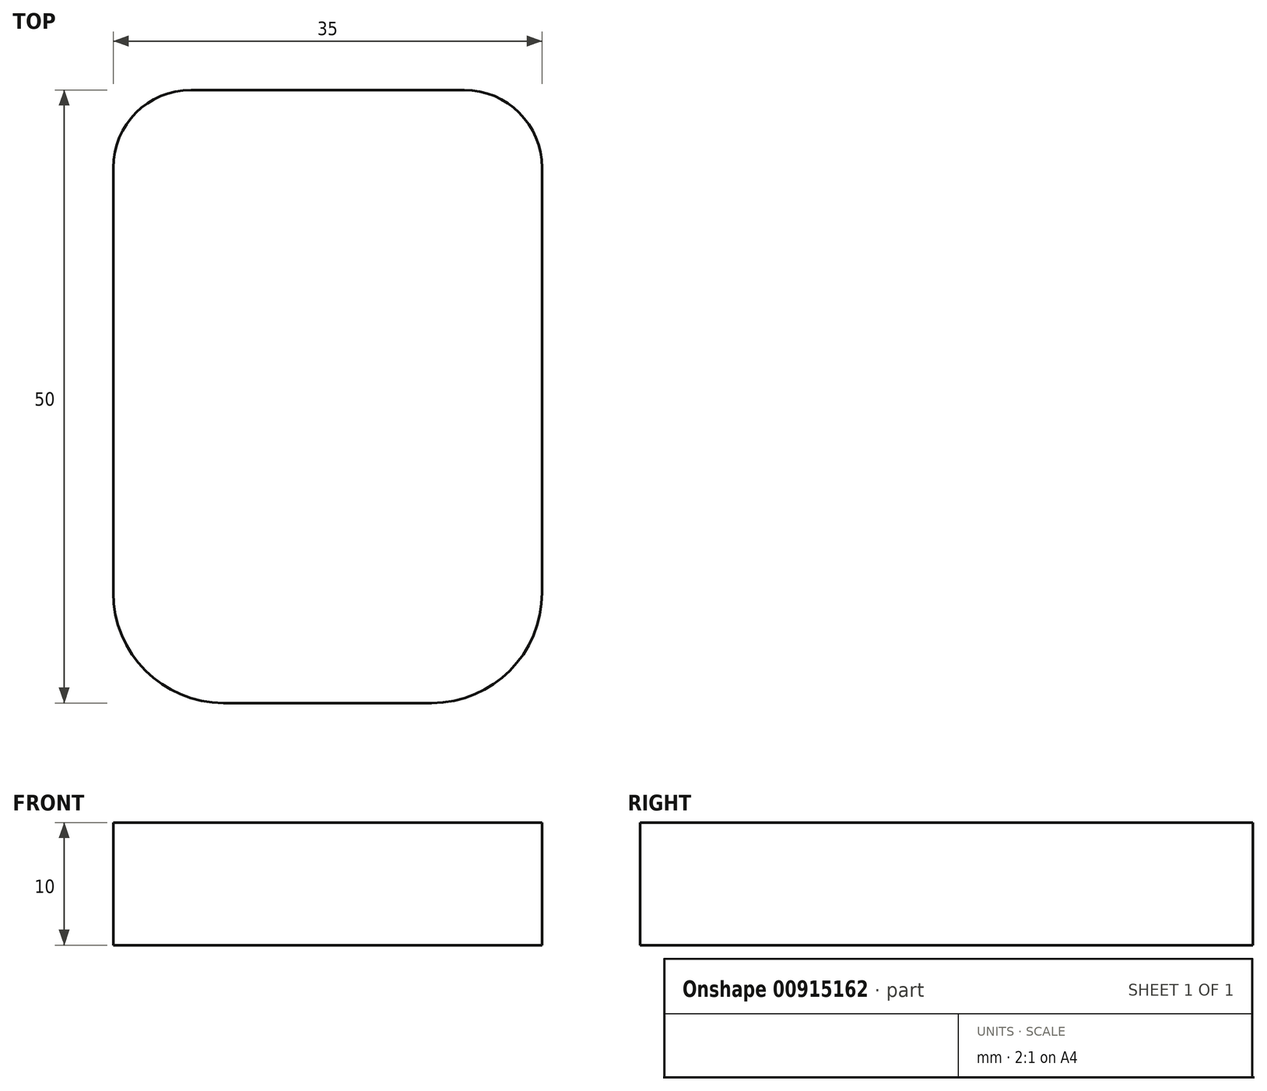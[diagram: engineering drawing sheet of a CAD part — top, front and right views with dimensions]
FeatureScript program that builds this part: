
annotation { "Feature Type Name" : "Feature", "Feature Type Description" : "" }
export const myFeature = defineFeature(function(context is Context, id is Id, definition is map)
    precondition{}
    {
        {
            var Q0;
            Q0=qCreatedBy(makeId("Top.planeOp"),FACE);
            var sketch = newSketch(context, id + "F0", { "sketchPlane" : qUnion([Q0])});
            skLineSegment(sketch, "E0.bottom", {"start": v(-28.65, 50) * mm, "end": v(-6.35, 50) * mm});
            skLineSegment(sketch, "E0.top", {"start": v(-26, 0) * mm, "end": v(-9, 0) * mm});
            skLineSegment(sketch, "E0.left", {"start": v(-35, 43.65) * mm, "end": v(-35, 9) * mm});
            skLineSegment(sketch, "E0.right", {"start": v(0, 43.65) * mm, "end": v(0, 9) * mm});
            skPoint(sketch, "E1.visualSharp", {"position": v(-35, 50) * mm});
            skArc(sketch, "E1.filletArc", {"start": v(-28.65, 50) * mm, "mid": v(-33.14, 48.14) * mm, "end": v(-35, 43.65) * mm});
            skPoint(sketch, "E2.visualSharp", {"position": v(0, 50) * mm});
            skArc(sketch, "E2.filletArc", {"start": v(0, 43.65) * mm, "mid": v(-1.86, 48.14) * mm, "end": v(-6.35, 50) * mm});
            skPoint(sketch, "E3.visualSharp", {"position": v(0, 0) * mm});
            skArc(sketch, "E3.filletArc", {"start": v(-9, 0) * mm, "mid": v(-2.64, 2.64) * mm, "end": v(0, 9) * mm});
            skPoint(sketch, "E4.visualSharp", {"position": v(-35, 0) * mm});
            skArc(sketch, "E4.filletArc", {"start": v(-35, 9) * mm, "mid": v(-32.36, 2.64) * mm, "end": v(-26, 0) * mm});
            skSolve(sketch);
        }
        {
            var Q0;
            Q0=makeQuery(id+"F0.imprint","IMPRINT",FACE,{"disambiguationData":[TD([[makeQuery(id+"F0.imprint","IMPRINT",EDGE,{"derivedFrom":sQuery(id+"F0.wireOp",EDGE,"E0.bottom")}),-1.0]])]});
            extrude(context, id + "F1", {"entities" : qUnion([Q0]), "depth" : 10 * mm, "offsetDistance" : 25 * mm});
        }
    });
